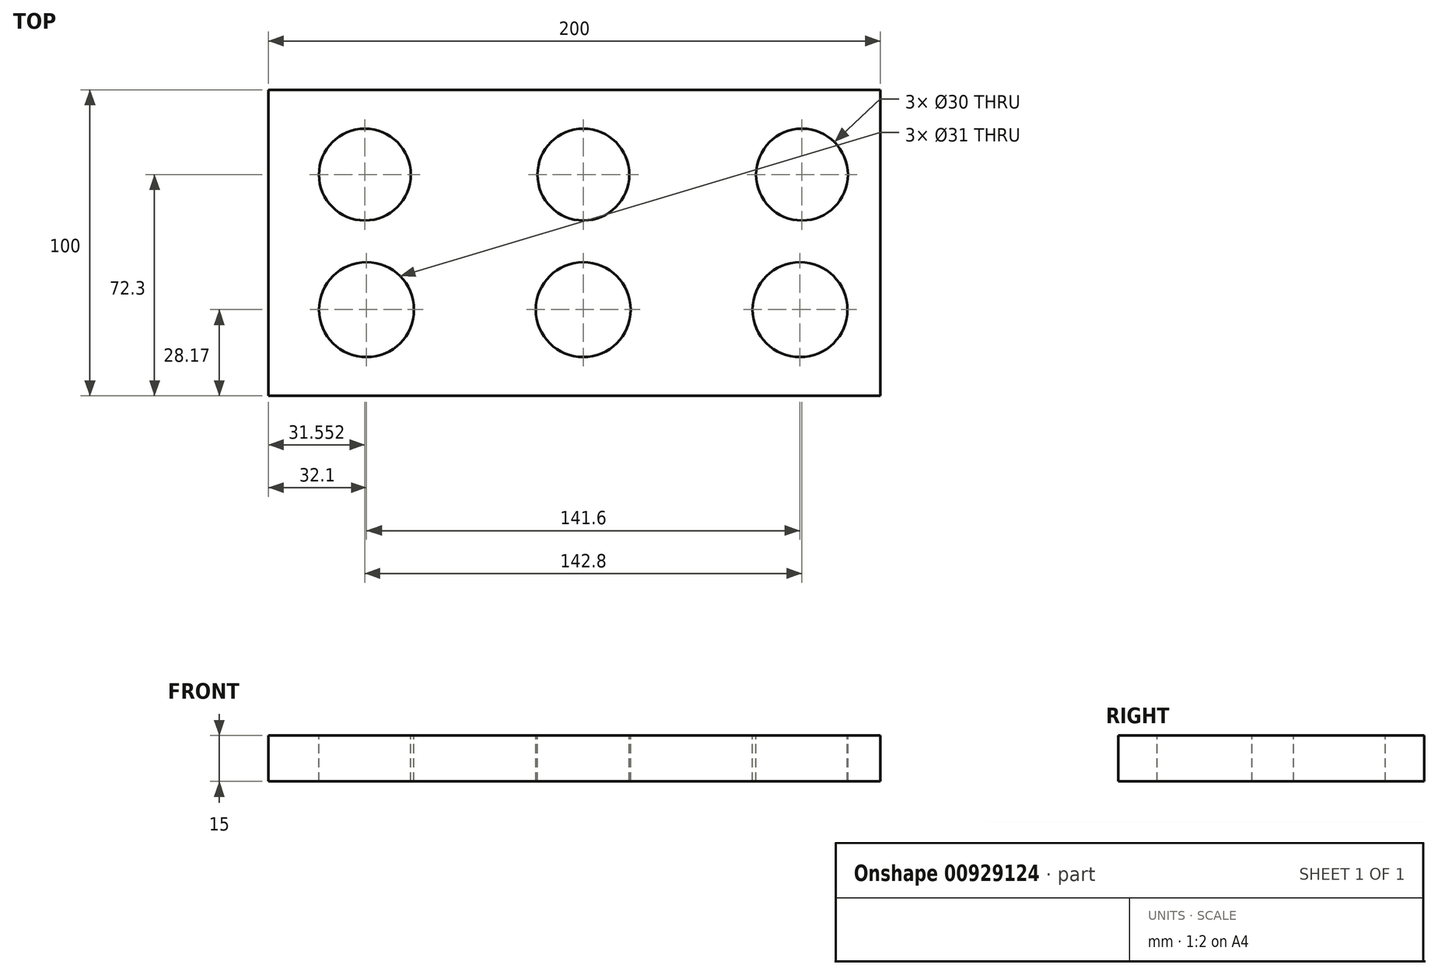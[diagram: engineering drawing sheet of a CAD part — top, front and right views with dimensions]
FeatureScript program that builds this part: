
annotation { "Feature Type Name" : "Feature", "Feature Type Description" : "" }
export const myFeature = defineFeature(function(context is Context, id is Id, definition is map)
    precondition{}
    {
        {
            var Q0;
            Q0=qCreatedBy(makeId("Top.planeOp"),FACE);
            var sketch = newSketch(context, id + "F0", { "sketchPlane" : qUnion([Q0])});
            skLineSegment(sketch, "E0.bottom", {"start": v(-99.26, 27.7) * mm, "end": v(100.74, 27.7) * mm});
            skLineSegment(sketch, "E0.top", {"start": v(-99.26, -72.3) * mm, "end": v(100.74, -72.3) * mm});
            skLineSegment(sketch, "E0.left", {"start": v(-99.26, 27.7) * mm, "end": v(-99.26, -72.3) * mm});
            skLineSegment(sketch, "E0.right", {"start": v(100.74, 27.7) * mm, "end": v(100.74, -72.3) * mm});
            skSolve(sketch);
        }
        {
            var Q0;
            Q0 = qSketchRegion(id + "F0", true);
            extrude(context, id + "F1", {"entities" : qUnion([Q0]), "depth" : 15 * mm, "offsetDistance" : 25 * mm});
        }
        {
            var Q0;
            Q0=makeQuery(id+"F1.opExtrude","CAP_FACE",FACE,{"disambiguationData":[OSD([sQuery(id+"F0.wireOp",EDGE,"E0.bottom"),sQuery(id+"F0.wireOp",EDGE,"E0.top"),sQuery(id+"F0.wireOp",EDGE,"E0.left"),sQuery(id+"F0.wireOp",EDGE,"E0.right")])],"isStart":false});
            var sketch = newSketch(context, id + "F2", { "sketchPlane" : qUnion([Q0])});
            skCircle(sketch, "E1", {"center": v(-67.7, 0) * mm, "radius": 15 * mm});
            skCircle(sketch, "E2.1.0.0", {"center": v(3.7, 0) * mm, "radius": 15 * mm});
            skCircle(sketch, "E2.2.0.0", {"center": v(75.1, 0) * mm, "radius": 15 * mm});
            skLineSegment(sketch, "E2.direction1", {"start": v(-67.7, 0) * mm, "end": v(3.7, 0) * mm, "construction": true});
            skSolve(sketch);
        }
        {
            var Q0;
            Q0=makeQuery(id+"F2.imprint","IMPRINT",FACE,{"disambiguationData":[TD([[makeQuery(id+"F2.imprint","IMPRINT",EDGE,{"derivedFrom":sQuery(id+"F2.wireOp",EDGE,"E1")}),1.0]])]});
            var Q1;
            Q1=makeQuery(id+"F2.imprint","IMPRINT",FACE,{"disambiguationData":[TD([[makeQuery(id+"F2.imprint","IMPRINT",EDGE,{"derivedFrom":sQuery(id+"F2.wireOp",EDGE,"E2.1.0.0")}),1.0]])]});
            var Q2;
            Q2=makeQuery(id+"F2.imprint","IMPRINT",FACE,{"disambiguationData":[TD([[makeQuery(id+"F2.imprint","IMPRINT",EDGE,{"derivedFrom":sQuery(id+"F2.wireOp",EDGE,"E2.2.0.0")}),1.0]])]});
            extrude(context, id + "F3", {"entities" : qUnion([Q0, Q1, Q2]), "operationType" : NewBodyOperationType.REMOVE, "endBound" : BoundingType.THROUGH_ALL, "oppositeDirection" : true, "depth" : 25 * mm, "offsetDistance" : 25 * mm});
        }
        {
            var Q0;
            Q0=makeQuery(id+"F1.opExtrude","CAP_FACE",FACE,{"disambiguationData":[OSD([sQuery(id+"F0.wireOp",EDGE,"E0.bottom"),sQuery(id+"F0.wireOp",EDGE,"E0.top"),sQuery(id+"F0.wireOp",EDGE,"E0.left"),sQuery(id+"F0.wireOp",EDGE,"E0.right")])],"isStart":false});
            var sketch = newSketch(context, id + "F4", { "sketchPlane" : qUnion([Q0])});
            skCircle(sketch, "E3", {"center": v(-67.16, -44.13) * mm, "radius": 15.5 * mm});
            skCircle(sketch, "E4.1.0.0", {"center": v(3.64, -44.13) * mm, "radius": 15.5 * mm});
            skCircle(sketch, "E4.2.0.0", {"center": v(74.44, -44.13) * mm, "radius": 15.5 * mm});
            skLineSegment(sketch, "E4.direction1", {"start": v(-67.16, -44.13) * mm, "end": v(3.64, -44.13) * mm, "construction": true});
            skSolve(sketch);
        }
        {
            var Q0;
            Q0=makeQuery(id+"F4.imprint","IMPRINT",FACE,{"disambiguationData":[TD([[makeQuery(id+"F4.imprint","IMPRINT",EDGE,{"derivedFrom":sQuery(id+"F4.wireOp",EDGE,"E3")}),1.0]])]});
            extrude(context, id + "F5", {"entities" : qUnion([Q0]), "operationType" : NewBodyOperationType.REMOVE, "endBound" : BoundingType.THROUGH_ALL, "oppositeDirection" : true, "depth" : 25 * mm, "offsetDistance" : 25 * mm});
        }
        {
            var Q0;
            Q0=makeQuery(id+"F4.imprint","IMPRINT",FACE,{"disambiguationData":[TD([[makeQuery(id+"F4.imprint","IMPRINT",EDGE,{"derivedFrom":sQuery(id+"F4.wireOp",EDGE,"E3")}),1.0]])]});
            var Q1;
            Q1=makeQuery(id+"F4.imprint","IMPRINT",FACE,{"disambiguationData":[TD([[makeQuery(id+"F4.imprint","IMPRINT",EDGE,{"derivedFrom":sQuery(id+"F4.wireOp",EDGE,"E4.1.0.0")}),1.0]])]});
            var Q2;
            Q2=makeQuery(id+"F4.imprint","IMPRINT",FACE,{"disambiguationData":[TD([[makeQuery(id+"F4.imprint","IMPRINT",EDGE,{"derivedFrom":sQuery(id+"F4.wireOp",EDGE,"E4.2.0.0")}),1.0]])]});
            extrude(context, id + "F6", {"entities" : qUnion([Q0, Q1, Q2]), "operationType" : NewBodyOperationType.REMOVE, "endBound" : BoundingType.THROUGH_ALL, "oppositeDirection" : true, "depth" : 25 * mm, "offsetDistance" : 25 * mm});
        }
    });
